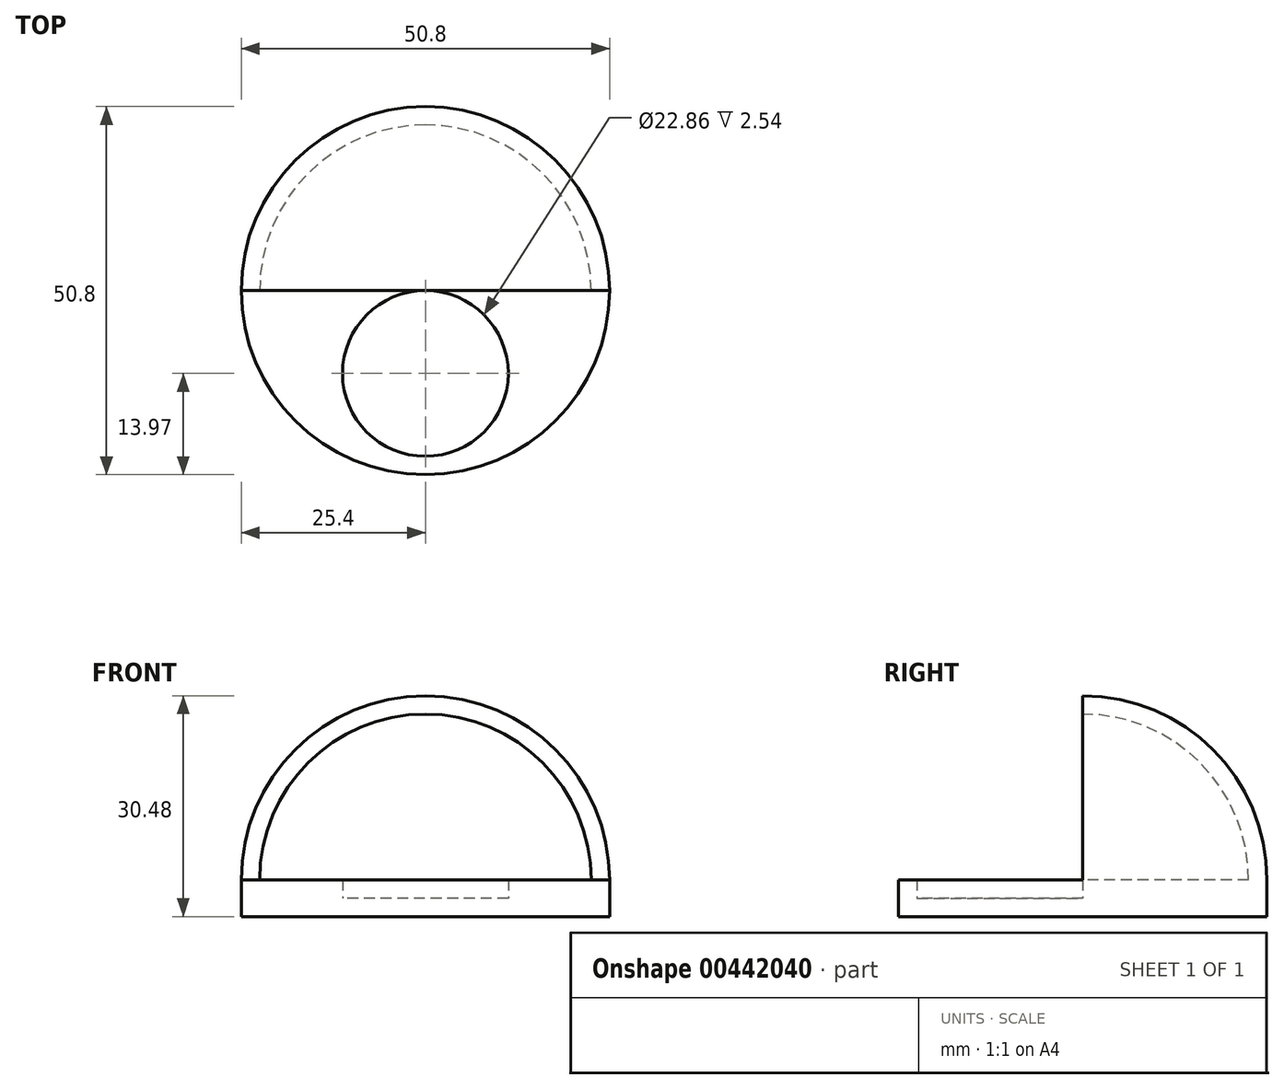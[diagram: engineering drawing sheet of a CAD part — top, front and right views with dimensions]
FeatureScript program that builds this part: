
annotation { "Feature Type Name" : "Feature", "Feature Type Description" : "" }
export const myFeature = defineFeature(function(context is Context, id is Id, definition is map)
    precondition{}
    {
        {
            var Q0;
            Q0=qCreatedBy(makeId("Top.planeOp"),FACE);
            var sketch = newSketch(context, id + "F0", { "sketchPlane" : qUnion([Q0])});
            skCircle(sketch, "E0", {"center": v(0, 0) * mm, "radius": 25.4 * mm});
            skCircle(sketch, "E1", {"center": v(0, -11.43) * mm, "radius": 11.43 * mm});
            skSolve(sketch);
        }
        {
            var Q0;
            Q0 = qSketchRegion(id + "F0", true);
            extrude(context, id + "F1", {"entities" : qUnion([Q0]), "depth" : 5.08 * mm});
        }
        {
            var Q0;
            Q0=makeQuery(id+"F0.imprint","IMPRINT",FACE,{"disambiguationData":[TD([[makeQuery(id+"F0.imprint","IMPRINT",EDGE,{"derivedFrom":sQuery(id+"F0.wireOp",EDGE,"E1")}),1.0]])]});
            extrude(context, id + "F2", {"entities" : qUnion([Q0]), "operationType" : NewBodyOperationType.ADD, "depth" : 2.54 * mm});
        }
        {
            var Q0;
            Q0=makeQuery(id+"F1.opExtrude","CAP_FACE",FACE,{"disambiguationData":[OSD([sQuery(id+"F0.wireOp",EDGE,"E0"),sQuery(id+"F0.wireOp",EDGE,"E1")])],"isStart":false});
            var sketch = newSketch(context, id + "F3", { "sketchPlane" : qUnion([Q0])});
            skCircle(sketch, "E2", {"center": v(0, 0) * mm, "radius": 25.4 * mm});
            skCircle(sketch, "E3", {"center": v(0, 0) * mm, "radius": 22.86 * mm});
            skLineSegment(sketch, "E4", {"start": v(0, 25.4) * mm, "end": v(0, 22.86) * mm});
            skLineSegment(sketch, "E5", {"start": v(0, 0) * mm, "end": v(25.4, 0) * mm});
            skSolve(sketch);
        }
        {
            var Q0;
            {var subQ0=sQuery(id+"F3.wireOp",EDGE,"E4");Q0=makeQuery(id+"F3.imprint","IMPRINT",FACE,{"disambiguationData":[TD([[makeQuery(id+"F3.imprint","IMPRINT",EDGE,{"derivedFrom":subQ0}),1.0]])]});}
            var Q1;
            Q1=sQuery(id+"F3.wireOp",EDGE,"E4");
            revolve(context, id + "F4", {"operationType" : NewBodyOperationType.ADD, "entities" : qUnion([Q0]), "axis" : qUnion([Q1]), "revolveType" : RevolveType.ONE_DIRECTION, "angle" : 180 * degree});
        }
    });
